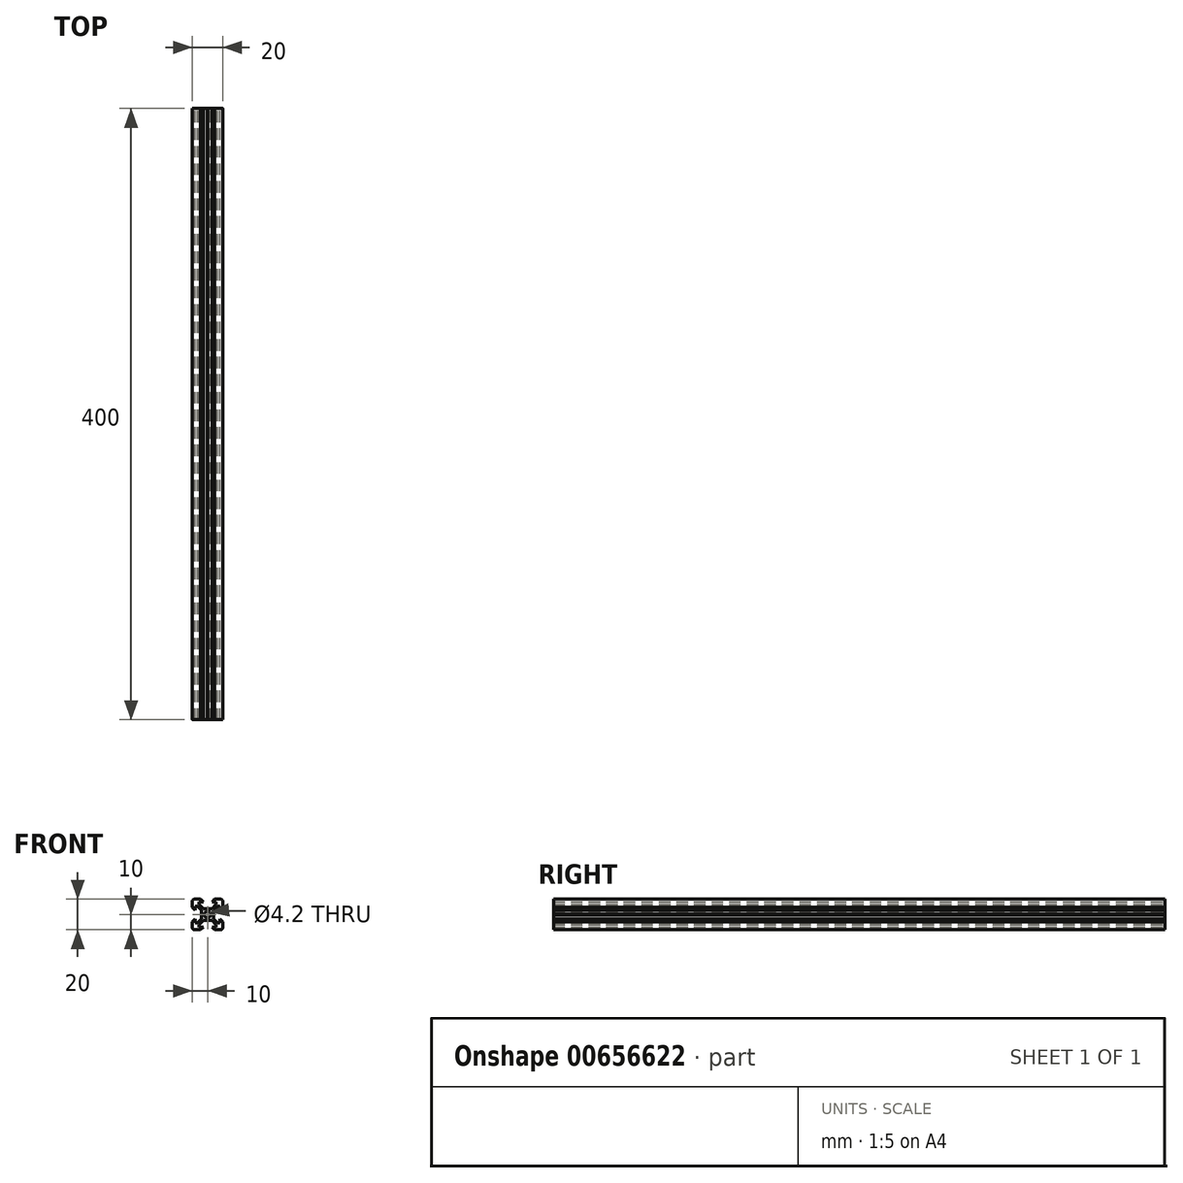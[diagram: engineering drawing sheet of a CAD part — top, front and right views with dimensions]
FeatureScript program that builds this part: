
annotation { "Feature Type Name" : "Feature", "Feature Type Description" : "" }
export const myFeature = defineFeature(function(context is Context, id is Id, definition is map)
    precondition{}
    {
        {
            var Q0;
            Q0=qCreatedBy(makeId("Front.planeOp"),FACE);
            var sketch = newSketch(context, id + "F0", { "sketchPlane" : qUnion([Q0])});
            skArc(sketch, "E0", {"start": v(-8.5, 10) * mm, "mid": v(-9.56, 9.56) * mm, "end": v(-10, 8.5) * mm});
            skLineSegment(sketch, "E1", {"start": v(-10, 8.5) * mm, "end": v(-10, 4.64) * mm});
            skLineSegment(sketch, "E2", {"start": v(-10, 4.64) * mm, "end": v(-8.2, 2.84) * mm});
            skLineSegment(sketch, "E3", {"start": v(-8.2, 5.5) * mm, "end": v(-8.2, 2.84) * mm});
            skLineSegment(sketch, "E4", {"start": v(-8.2, 5.5) * mm, "end": v(-6.56, 5.5) * mm});
            skLineSegment(sketch, "E5", {"start": v(-6.56, 5.5) * mm, "end": v(-3.9, 2.84) * mm});
            skLineSegment(sketch, "E6", {"start": v(-3.9, 2.84) * mm, "end": v(-3.9, 0.2) * mm});
            skLineSegment(sketch, "E7", {"start": v(-3.9, 0.2) * mm, "end": v(-3.7, 0) * mm});
            skLineSegment(sketch, "E8", {"start": v(-3.9, -0.2) * mm, "end": v(-3.7, 0) * mm});
            skLineSegment(sketch, "E9", {"start": v(-3.9, -2.84) * mm, "end": v(-3.9, -0.2) * mm});
            skLineSegment(sketch, "E10", {"start": v(-6.56, -5.5) * mm, "end": v(-3.9, -2.84) * mm});
            skLineSegment(sketch, "E11", {"start": v(-8.2, -5.5) * mm, "end": v(-6.56, -5.5) * mm});
            skLineSegment(sketch, "E12", {"start": v(-8.2, -5.5) * mm, "end": v(-8.2, -2.84) * mm});
            skLineSegment(sketch, "E13", {"start": v(-10, -4.64) * mm, "end": v(-8.2, -2.84) * mm});
            skLineSegment(sketch, "E14", {"start": v(-10, -8.5) * mm, "end": v(-10, -4.64) * mm});
            skArc(sketch, "E15", {"start": v(-10, -8.5) * mm, "mid": v(-9.56, -9.56) * mm, "end": v(-8.5, -10) * mm});
            skLineSegment(sketch, "E16", {"start": v(-8.5, -10) * mm, "end": v(-4.64, -10) * mm});
            skLineSegment(sketch, "E17", {"start": v(-4.64, -10) * mm, "end": v(-2.84, -8.2) * mm});
            skLineSegment(sketch, "E18", {"start": v(-2.84, -8.2) * mm, "end": v(-5.5, -8.2) * mm});
            skLineSegment(sketch, "E19", {"start": v(-5.5, -8.2) * mm, "end": v(-5.5, -6.56) * mm});
            skLineSegment(sketch, "E20", {"start": v(-5.5, -6.56) * mm, "end": v(-2.84, -3.9) * mm});
            skLineSegment(sketch, "E21", {"start": v(-0.2, -3.9) * mm, "end": v(-2.84, -3.9) * mm});
            skLineSegment(sketch, "E22", {"start": v(-0.2, -3.9) * mm, "end": v(0, -3.7) * mm});
            skLineSegment(sketch, "E23", {"start": v(0.2, -3.9) * mm, "end": v(0, -3.7) * mm});
            skLineSegment(sketch, "E24", {"start": v(0.2, -3.9) * mm, "end": v(2.84, -3.9) * mm});
            skLineSegment(sketch, "E25", {"start": v(5.5, -6.56) * mm, "end": v(2.84, -3.9) * mm});
            skLineSegment(sketch, "E26", {"start": v(5.5, -8.2) * mm, "end": v(5.5, -6.56) * mm});
            skLineSegment(sketch, "E27", {"start": v(2.84, -8.2) * mm, "end": v(5.5, -8.2) * mm});
            skLineSegment(sketch, "E28", {"start": v(4.64, -10) * mm, "end": v(2.84, -8.2) * mm});
            skLineSegment(sketch, "E29", {"start": v(8.5, -10) * mm, "end": v(4.64, -10) * mm});
            skArc(sketch, "E30", {"start": v(8.5, -10) * mm, "mid": v(9.56, -9.56) * mm, "end": v(10, -8.5) * mm});
            skLineSegment(sketch, "E31", {"start": v(10, -8.5) * mm, "end": v(10, -4.64) * mm});
            skLineSegment(sketch, "E32", {"start": v(10, -4.64) * mm, "end": v(8.2, -2.84) * mm});
            skLineSegment(sketch, "E33", {"start": v(8.2, -5.5) * mm, "end": v(8.2, -2.84) * mm});
            skLineSegment(sketch, "E34", {"start": v(8.2, -5.5) * mm, "end": v(6.56, -5.5) * mm});
            skLineSegment(sketch, "E35", {"start": v(6.56, -5.5) * mm, "end": v(3.9, -2.84) * mm});
            skLineSegment(sketch, "E36", {"start": v(3.9, -2.84) * mm, "end": v(3.9, -0.2) * mm});
            skLineSegment(sketch, "E37", {"start": v(3.9, -0.2) * mm, "end": v(3.7, 0) * mm});
            skLineSegment(sketch, "E38", {"start": v(3.9, 0.2) * mm, "end": v(3.7, 0) * mm});
            skLineSegment(sketch, "E39", {"start": v(3.9, 2.84) * mm, "end": v(3.9, 0.2) * mm});
            skLineSegment(sketch, "E40", {"start": v(6.56, 5.5) * mm, "end": v(3.9, 2.84) * mm});
            skLineSegment(sketch, "E41", {"start": v(8.2, 5.5) * mm, "end": v(6.56, 5.5) * mm});
            skLineSegment(sketch, "E42", {"start": v(8.2, 5.5) * mm, "end": v(8.2, 2.84) * mm});
            skLineSegment(sketch, "E43", {"start": v(10, 4.64) * mm, "end": v(8.2, 2.84) * mm});
            skLineSegment(sketch, "E44", {"start": v(10, 8.5) * mm, "end": v(10, 4.64) * mm});
            skArc(sketch, "E45", {"start": v(10, 8.5) * mm, "mid": v(9.56, 9.56) * mm, "end": v(8.5, 10) * mm});
            skLineSegment(sketch, "E46", {"start": v(8.5, 10) * mm, "end": v(4.64, 10) * mm});
            skLineSegment(sketch, "E47", {"start": v(4.64, 10) * mm, "end": v(2.84, 8.2) * mm});
            skLineSegment(sketch, "E48", {"start": v(2.84, 8.2) * mm, "end": v(5.5, 8.2) * mm});
            skLineSegment(sketch, "E49", {"start": v(5.5, 8.2) * mm, "end": v(5.5, 6.56) * mm});
            skLineSegment(sketch, "E50", {"start": v(5.5, 6.56) * mm, "end": v(2.84, 3.9) * mm});
            skLineSegment(sketch, "E51", {"start": v(0.2, 3.9) * mm, "end": v(2.84, 3.9) * mm});
            skLineSegment(sketch, "E52", {"start": v(0.2, 3.9) * mm, "end": v(0, 3.7) * mm});
            skLineSegment(sketch, "E53", {"start": v(-0.2, 3.9) * mm, "end": v(0, 3.7) * mm});
            skLineSegment(sketch, "E54", {"start": v(-0.2, 3.9) * mm, "end": v(-2.84, 3.9) * mm});
            skLineSegment(sketch, "E55", {"start": v(-5.5, 6.56) * mm, "end": v(-2.84, 3.9) * mm});
            skLineSegment(sketch, "E56", {"start": v(-5.5, 8.2) * mm, "end": v(-5.5, 6.56) * mm});
            skLineSegment(sketch, "E57", {"start": v(-2.84, 8.2) * mm, "end": v(-5.5, 8.2) * mm});
            skLineSegment(sketch, "E58", {"start": v(-4.64, 10) * mm, "end": v(-2.84, 8.2) * mm});
            skLineSegment(sketch, "E59", {"start": v(-8.5, 10) * mm, "end": v(-4.64, 10) * mm});
            skCircle(sketch, "E60", {"center": v(0, 0) * mm, "radius": 2.1 * mm});
            skSolve(sketch);
        }
        {
            var Q0;
            Q0=qSketchRegion(id+"F0",true);
            extrude(context, id + "F1", {"entities" : qUnion([Q0]), "endBound" : BoundingType.SYMMETRIC, "depth" : 400 * mm, "offsetDistance" : 25.4 * mm});
        }
    });
